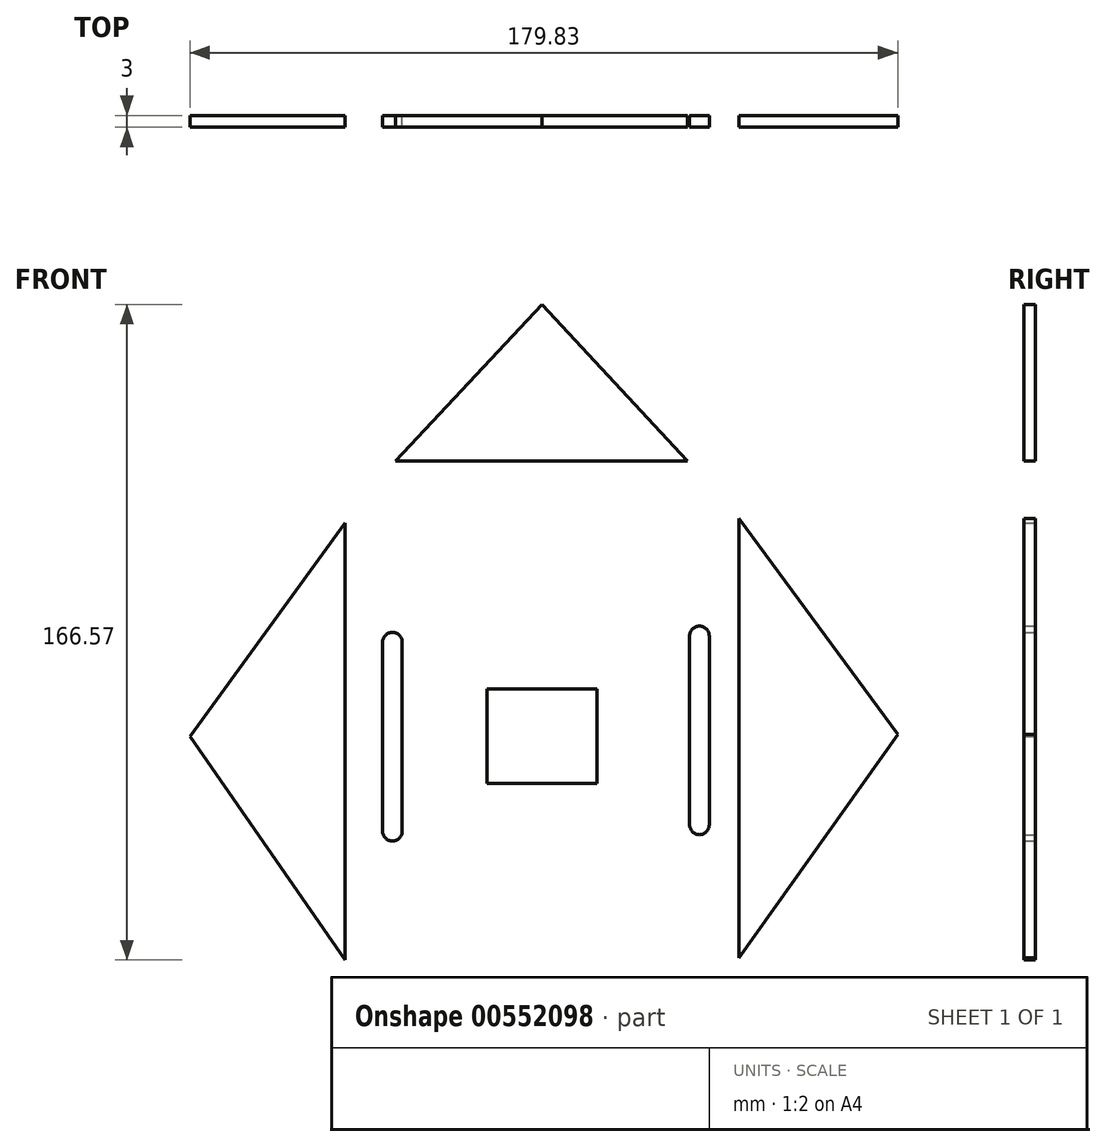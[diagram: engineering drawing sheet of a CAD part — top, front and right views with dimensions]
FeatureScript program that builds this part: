
annotation { "Feature Type Name" : "Feature", "Feature Type Description" : "" }
export const myFeature = defineFeature(function(context is Context, id is Id, definition is map)
    precondition{}
    {
        {
            var Q0;
            Q0=qCreatedBy(makeId("Front.planeOp"),FACE);
            var sketch = newSketch(context, id + "F0", { "sketchPlane" : qUnion([Q0])});
            skLineSegment(sketch, "E0.bottom", {"start": v(-37.3, 70) * mm, "end": v(37.3, 70) * mm});
            skLineSegment(sketch, "E0.top", {"start": v(-37.3, -70) * mm, "end": v(37.3, -70) * mm});
            skLineSegment(sketch, "E0.left", {"start": v(-50, 57.3) * mm, "end": v(-50, -57.3) * mm});
            skLineSegment(sketch, "E0.right", {"start": v(50, 57.3) * mm, "end": v(50, -57.3) * mm});
            skPoint(sketch, "E0.middle", {"position": v(0, 0) * mm});
            skLineSegment(sketch, "E1", {"start": v(39.97, 25.54) * mm, "end": v(39.97, -22.46) * mm});
            skPoint(sketch, "E2", {"position": v(32.04, 15.14) * mm});
            skPoint(sketch, "E3", {"position": v(31.72, -9.28) * mm});
            skPoint(sketch, "E4", {"position": v(-27.1, -9.28) * mm});
            skPoint(sketch, "E5", {"position": v(-26.78, 15.14) * mm});
            skLineSegment(sketch, "E6", {"start": v(-38.03, 23.93) * mm, "end": v(-38.03, -24.07) * mm});
            skPoint(sketch, "E7.visualSharp", {"position": v(50, 70) * mm});
            skArc(sketch, "E7.filletArc", {"start": v(50, 57.3) * mm, "mid": v(46.28, 66.28) * mm, "end": v(37.3, 70) * mm});
            skPoint(sketch, "E8.visualSharp", {"position": v(-50, 70) * mm});
            skArc(sketch, "E8.filletArc", {"start": v(-37.3, 70) * mm, "mid": v(-46.28, 66.28) * mm, "end": v(-50, 57.3) * mm});
            skPoint(sketch, "E9.visualSharp", {"position": v(-50, -70) * mm});
            skArc(sketch, "E9.filletArc", {"start": v(-50, -57.3) * mm, "mid": v(-46.28, -66.28) * mm, "end": v(-37.3, -70) * mm});
            skPoint(sketch, "E10.visualSharp", {"position": v(50, -70) * mm});
            skArc(sketch, "E10.filletArc", {"start": v(37.3, -70) * mm, "mid": v(46.28, -66.28) * mm, "end": v(50, -57.3) * mm});
            skSolve(sketch);
        }
        {
            var Q0;
            Q0=makeQuery(id+"F0.imprint","IMPRINT",FACE,{"disambiguationData":[TD([[makeQuery(id+"F0.imprint","IMPRINT",EDGE,{"derivedFrom":sQuery(id+"F0.wireOp",EDGE,"E0.bottom")}),-1.0]])]});
            var sketch = newSketch(context, id + "F1", { "sketchPlane" : qUnion([Q0])});
            skLineSegment(sketch, "E11.JFR.JFR", {"start": v(39.97, 25.54) * mm, "end": v(39.97, -22.46) * mm, "construction": true});
            skLineSegment(sketch, "E11.JFV.JFV", {"start": v(-38.03, 23.93) * mm, "end": v(-38.03, -24.07) * mm, "construction": true});
            skArc(sketch, "E11.0.startCap", {"start": v(37.47, 25.54) * mm, "mid": v(39.97, 28.04) * mm, "end": v(42.47, 25.54) * mm});
            skArc(sketch, "E11.0.endCap", {"start": v(42.47, -22.46) * mm, "mid": v(39.97, -24.96) * mm, "end": v(37.47, -22.46) * mm});
            skLineSegment(sketch, "E11.0.left", {"start": v(42.47, 25.54) * mm, "end": v(42.47, -22.46) * mm});
            skLineSegment(sketch, "E11.0.right", {"start": v(37.47, 25.54) * mm, "end": v(37.47, -22.46) * mm});
            skArc(sketch, "E11.1.startCap", {"start": v(-40.53, 23.93) * mm, "mid": v(-38.03, 26.43) * mm, "end": v(-35.53, 23.93) * mm});
            skArc(sketch, "E11.1.endCap", {"start": v(-35.53, -24.07) * mm, "mid": v(-38.03, -26.57) * mm, "end": v(-40.53, -24.07) * mm});
            skLineSegment(sketch, "E11.1.left", {"start": v(-35.53, 23.93) * mm, "end": v(-35.53, -24.07) * mm});
            skLineSegment(sketch, "E11.1.right", {"start": v(-40.53, 23.93) * mm, "end": v(-40.53, -24.07) * mm});
            skLineSegment(sketch, "E12", {"start": v(37.17, 69.75) * mm, "end": v(0, 109.76) * mm});
            skLineSegment(sketch, "E13", {"start": v(-37.36, 69.93) * mm, "end": v(0, 109.76) * mm});
            skLineSegment(sketch, "E14", {"start": v(-48.37, 56.48) * mm, "end": v(-89.47, 0) * mm});
            skLineSegment(sketch, "E15", {"start": v(-49.61, -57.36) * mm, "end": v(-89.47, 0) * mm});
            skLineSegment(sketch, "E16", {"start": v(48.95, 56.8) * mm, "end": v(90.36, 0.55) * mm});
            skLineSegment(sketch, "E17", {"start": v(49.9, -56.4) * mm, "end": v(90.36, 0.55) * mm});
            skSolve(sketch);
        }
        {
            var Q0;
            {var subQ0=sQuery(id+"F1.wireOp",EDGE,"E15");var subQ1=sQuery(id+"F1.wireOp",EDGE,"E14");var subQ2=makeQuery(id+"F1.imprint","INTERSECT",VERTEX,{"derivedFrom":[subQ1,subQ0]});Q0=makeQuery(id+"F1.imprint","IMPRINT",FACE,{"disambiguationData":[TD([[makeQuery(id+"F1.imprint","IMPRINT",EDGE,{"disambiguationData":[TD([[subQ2,1.0]])],"derivedFrom":subQ1}),1.0]])]});}
            var Q1;
            Q1=makeQuery(id+"F0.imprint","IMPRINT",FACE,{"disambiguationData":[TD([[makeQuery(id+"F0.imprint","IMPRINT",EDGE,{"derivedFrom":sQuery(id+"F0.wireOp",EDGE,"E0.bottom")}),-1.0]])]});
            extrude(context, id + "F2", {"entities" : qUnion([Q0, Q1]), "depth" : 3 * mm, "offsetDistance" : 25.4 * mm});
        }
        {
            var Q0;
            Q0=makeQuery(id+"F1.imprint","IMPRINT",FACE,{"disambiguationData":[TD([[makeQuery(id+"F1.imprint","IMPRINT",EDGE,{"derivedFrom":sQuery(id+"F1.wireOp",EDGE,"E11.1.startCap")}),-1.0]])]});
            var Q1;
            Q1=makeQuery(id+"F1.imprint","IMPRINT",FACE,{"disambiguationData":[TD([[makeQuery(id+"F1.imprint","IMPRINT",EDGE,{"derivedFrom":sQuery(id+"F1.wireOp",EDGE,"E11.0.startCap")}),-1.0]])]});
            extrude(context, id + "F3", {"entities" : qUnion([Q0, Q1]), "operationType" : NewBodyOperationType.REMOVE, "depth" : 25.4 * mm, "offsetDistance" : 25.4 * mm});
        }
        {
            var Q0;
            {var subQ0=sQuery(id+"F1.wireOp",EDGE,"E13");var subQ1=sQuery(id+"F1.wireOp",EDGE,"E12");var subQ2=makeQuery(id+"F1.imprint","INTERSECT",VERTEX,{"derivedFrom":[subQ1,subQ0]});Q0=makeQuery(id+"F1.imprint","IMPRINT",FACE,{"disambiguationData":[TD([[makeQuery(id+"F1.imprint","IMPRINT",EDGE,{"disambiguationData":[TD([[subQ2,1.0]])],"derivedFrom":subQ1}),1.0]])]});}
            var Q1;
            {var subQ0=sQuery(id+"F1.wireOp",EDGE,"E17");var subQ1=sQuery(id+"F1.wireOp",EDGE,"E16");var subQ2=makeQuery(id+"F1.imprint","INTERSECT",VERTEX,{"derivedFrom":[subQ1,subQ0]});Q1=makeQuery(id+"F1.imprint","IMPRINT",FACE,{"disambiguationData":[TD([[makeQuery(id+"F1.imprint","IMPRINT",EDGE,{"disambiguationData":[TD([[subQ2,1.0]])],"derivedFrom":subQ1}),-1.0]])]});}
            extrude(context, id + "F4", {"entities" : qUnion([Q0, Q1]), "depth" : 3 * mm, "offsetDistance" : 25.4 * mm});
        }
        {
            var Q0;
            Q0=makeQuery(id+"F2.opExtrude","CAP_FACE",FACE,{"disambiguationData":[OSD([sQuery(id+"F0.wireOp",EDGE,"E0.bottom"),sQuery(id+"F0.wireOp",EDGE,"E0.top"),sQuery(id+"F0.wireOp",EDGE,"E0.left"),sQuery(id+"F0.wireOp",EDGE,"E0.right"),sQuery(id+"F0.wireOp",EDGE,"E7.filletArc"),sQuery(id+"F0.wireOp",EDGE,"E8.filletArc"),sQuery(id+"F0.wireOp",EDGE,"E9.filletArc"),sQuery(id+"F0.wireOp",EDGE,"E10.filletArc")])],"isStart":true});
            var sketch = newSketch(context, id + "F5", { "sketchPlane" : qUnion([Q0])});
            skLineSegment(sketch, "E18.bottom", {"start": v(14, 12) * mm, "end": v(-14, 12) * mm});
            skLineSegment(sketch, "E18.top", {"start": v(14, -12) * mm, "end": v(-14, -12) * mm});
            skLineSegment(sketch, "E18.left", {"start": v(14, 12) * mm, "end": v(14, -12) * mm});
            skLineSegment(sketch, "E18.right", {"start": v(-14, 12) * mm, "end": v(-14, -12) * mm});
            skPoint(sketch, "E18.middle", {"position": v(0, 0) * mm});
            skLineSegment(sketch, "E19", {"start": v(7.43, -7.13) * mm, "end": v(-6.06, -7.13) * mm});
            skLineSegment(sketch, "E20", {"start": v(-6.06, -7.13) * mm, "end": v(7.43, -7.13) * mm});
            skLineSegment(sketch, "E21", {"start": v(7.43, 6.48) * mm, "end": v(-4.91, 6.48) * mm});
            skLineSegment(sketch, "E22", {"start": v(-4.91, 6.48) * mm, "end": v(7.43, 6.48) * mm});
            skSolve(sketch);
        }
        {
            var Q0;
            Q0 = qSketchRegion(id + "F5", true);
            var sketch = newSketch(context, id + "F6", { "sketchPlane" : qUnion([Q0])});
            skLineSegment(sketch, "E23.JSZ.JSZ", {"start": v(-6.06, -7.13) * mm, "end": v(7.43, -7.13) * mm, "construction": true});
            skArc(sketch, "E23.0.startCap", {"start": v(-6.06, -8.4) * mm, "mid": v(-7.33, -7.13) * mm, "end": v(-6.06, -5.86) * mm});
            skArc(sketch, "E23.0.endCap", {"start": v(7.43, -5.86) * mm, "mid": v(8.7, -7.13) * mm, "end": v(7.43, -8.4) * mm});
            skLineSegment(sketch, "E23.0.left", {"start": v(-6.06, -5.86) * mm, "end": v(7.43, -5.86) * mm});
            skLineSegment(sketch, "E23.0.right", {"start": v(-6.06, -8.4) * mm, "end": v(7.43, -8.4) * mm});
            skLineSegment(sketch, "E24.JSh.JSh", {"start": v(-4.91, 6.48) * mm, "end": v(7.43, 6.48) * mm, "construction": true});
            skArc(sketch, "E24.0.startCap", {"start": v(-4.91, 5.21) * mm, "mid": v(-6.18, 6.48) * mm, "end": v(-4.91, 7.75) * mm});
            skArc(sketch, "E24.0.endCap", {"start": v(7.43, 7.75) * mm, "mid": v(8.7, 6.48) * mm, "end": v(7.43, 5.21) * mm});
            skLineSegment(sketch, "E24.0.left", {"start": v(-4.91, 7.75) * mm, "end": v(7.43, 7.75) * mm});
            skLineSegment(sketch, "E24.0.right", {"start": v(-4.91, 5.21) * mm, "end": v(7.43, 5.21) * mm});
            skSolve(sketch);
        }
        {
            var Q0;
            Q0=makeQuery(id+"F5.imprint","IMPRINT",FACE,{"disambiguationData":[TD([[makeQuery(id+"F5.imprint","IMPRINT",EDGE,{"derivedFrom":sQuery(id+"F5.wireOp",EDGE,"E18.bottom")}),1.0]])]});
            var Q1;
            Q1=sQuery(id+"F5.wireOp",EDGE,"E18.left");
            var Q2;
            Q2=sQuery(id+"F5.wireOp",EDGE,"E18.bottom");
            var Q3;
            Q3=sQuery(id+"F5.wireOp",EDGE,"E18.top");
            var Q4;
            Q4=sQuery(id+"F5.wireOp",EDGE,"E18.right");
            extrude(context, id + "F7", {"entities" : qUnion([Q0]), "operationType" : NewBodyOperationType.REMOVE, "surfaceEntities" : qUnion([Q1, Q2, Q3, Q4]), "oppositeDirection" : true, "depth" : 85.95 * mm, "offsetDistance" : 25.4 * mm});
        }
        {
            var Q0;
            Q0=makeQuery(id+"F5.imprint","IMPRINT",FACE,{"disambiguationData":[TD([[makeQuery(id+"F5.imprint","IMPRINT",EDGE,{"derivedFrom":sQuery(id+"F5.wireOp",EDGE,"E18.bottom")}),1.0]])]});
            extrude(context, id + "F8", {"entities" : qUnion([Q0]), "operationType" : NewBodyOperationType.ADD, "oppositeDirection" : true, "depth" : 0.58 * mm, "offsetDistance" : 25.4 * mm});
        }
        {
            var Q0;
            Q0=makeQuery(id+"F8.opExtrude","CAP_FACE",FACE,{"disambiguationData":[OSD([sQuery(id+"F5.wireOp",EDGE,"E18.bottom"),sQuery(id+"F5.wireOp",EDGE,"E18.top"),sQuery(id+"F5.wireOp",EDGE,"E18.left"),sQuery(id+"F5.wireOp",EDGE,"E18.right")])],"isStart":false});
            var Q1;
            Q1=makeQuery(id+"F6.imprint","IMPRINT",FACE,{"disambiguationData":[TD([[makeQuery(id+"F6.imprint","IMPRINT",EDGE,{"derivedFrom":sQuery(id+"F6.wireOp",EDGE,"E23.0.startCap")}),-1.0]])]});
            var Q2;
            Q2=makeQuery(id+"F6.imprint","IMPRINT",FACE,{"disambiguationData":[TD([[makeQuery(id+"F6.imprint","IMPRINT",EDGE,{"derivedFrom":sQuery(id+"F6.wireOp",EDGE,"E24.0.startCap")}),-1.0]])]});
            extrude(context, id + "F9", {"entities" : qUnion([Q0, Q1, Q2]), "operationType" : NewBodyOperationType.REMOVE, "oppositeDirection" : true, "depth" : 13.2 * mm, "offsetDistance" : 25.4 * mm});
        }
        {
            var Q0;
            Q0=makeQuery(id+"F5.imprint","IMPRINT",FACE,{"disambiguationData":[TD([[makeQuery(id+"F5.imprint","IMPRINT",EDGE,{"derivedFrom":sQuery(id+"F5.wireOp",EDGE,"E18.bottom")}),1.0]])]});
            extrude(context, id + "F10", {"entities" : qUnion([Q0]), "depth" : 0 * mm, "offsetDistance" : 25.4 * mm});
        }
        {
            var Q0;
            Q0=makeQuery(id+"F5.imprint","IMPRINT",FACE,{"disambiguationData":[TD([[makeQuery(id+"F5.imprint","IMPRINT",EDGE,{"derivedFrom":sQuery(id+"F5.wireOp",EDGE,"E18.bottom")}),1.0]])]});
            var sketch = newSketch(context, id + "F11", { "sketchPlane" : qUnion([Q0])});
            skPoint(sketch, "E25", {"position": v(0, -7.06) * mm});
            skPoint(sketch, "E26", {"position": v(0, 6.46) * mm});
            skSolve(sketch);
        }
        {
            var Q0;
            Q0=sQuery(id+"F5.wireOp",VERTEX,"E18.left.start");
            var Q1;
            Q1=sQuery(id+"F5.wireOp",VERTEX,"E18.top.start");
            var Q2;
            Q2=sQuery(id+"F5.wireOp",VERTEX,"E18.right.start");
            var Q3;
            Q3=sQuery(id+"F5.wireOp",VERTEX,"E18.right.end");
            var Q4;
            Q4=makeQuery(id+"F2.opExtrude","SWEPT_BODY",BODY,{"disambiguationData":[OSD([sQuery(id+"F0.wireOp",EDGE,"E0.bottom"),sQuery(id+"F0.wireOp",EDGE,"E0.top"),sQuery(id+"F0.wireOp",EDGE,"E0.left"),sQuery(id+"F0.wireOp",EDGE,"E0.right"),sQuery(id+"F0.wireOp",EDGE,"E7.filletArc"),sQuery(id+"F0.wireOp",EDGE,"E8.filletArc"),sQuery(id+"F0.wireOp",EDGE,"E9.filletArc"),sQuery(id+"F0.wireOp",EDGE,"E10.filletArc")])]});
            hole(context, id + "F12", {"style" : HoleStyle.SIMPLE, "endStyle" : HoleEndStyle.THROUGH, "holeDiameter" : 3 * mm, "isTappedThrough" : true, "tappedDepth" : 12.7 * mm, "tapClearance" : 3, "locations" : qUnion([Q0, Q1, Q2, Q3]), "scope" : qUnion([Q4])});
        }
        {
            var Q0;
            Q0=makeQuery(id+"F11.imprint","IMPRINT",FACE,{"disambiguationData":[TD([[makeQuery(id+"F11.imprint","IMPRINT",EDGE,{"derivedFrom":makeQuery(id+"F5.imprint","IMPRINT",EDGE,{"derivedFrom":sQuery(id+"F5.wireOp",EDGE,"E18.bottom")})}),1.0]])]});
            extrude(context, id + "F13", {"entities" : qUnion([Q0]), "operationType" : NewBodyOperationType.ADD, "depth" : 0 * mm, "offsetDistance" : 25.4 * mm});
        }
    });
